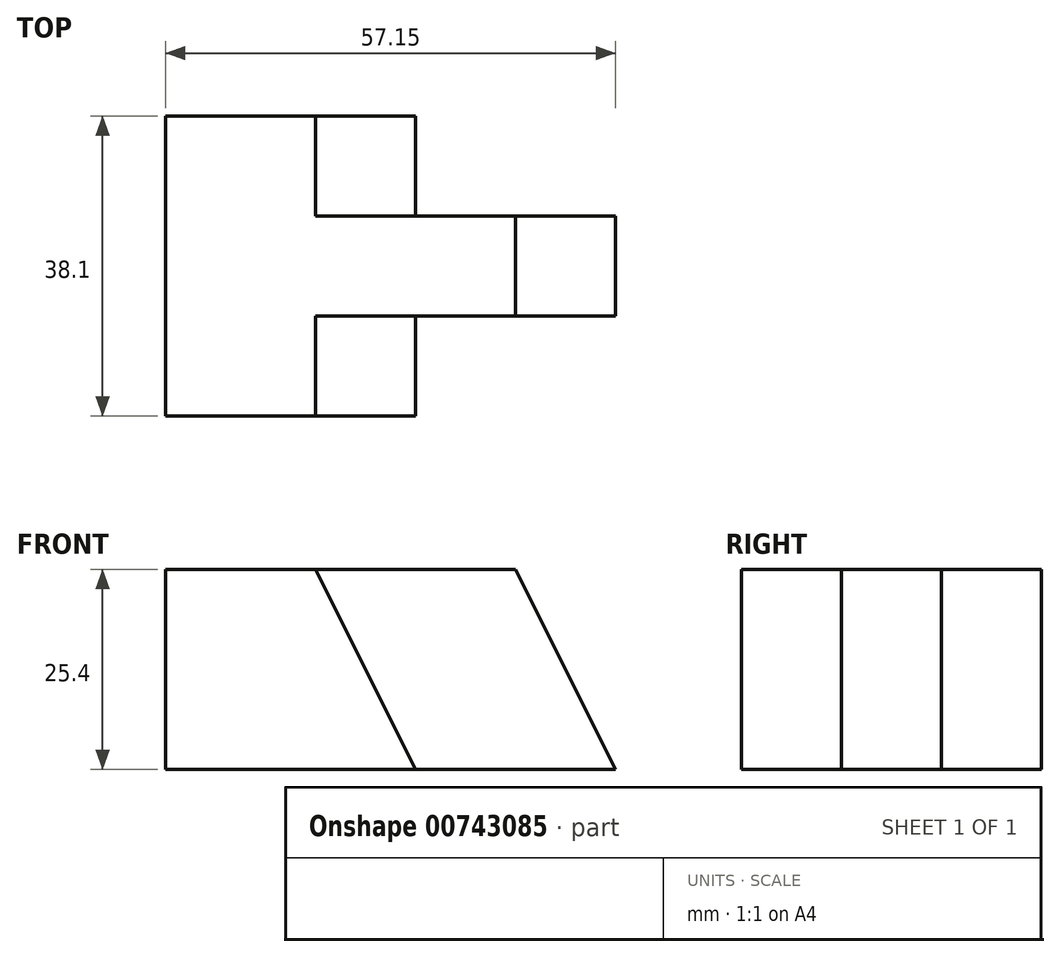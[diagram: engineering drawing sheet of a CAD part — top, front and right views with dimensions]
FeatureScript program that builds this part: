
annotation { "Feature Type Name" : "Feature", "Feature Type Description" : "" }
export const myFeature = defineFeature(function(context is Context, id is Id, definition is map)
    precondition{}
    {
        {
            var Q0;
            Q0=qCreatedBy(makeId("Front.planeOp"),FACE);
            var sketch = newSketch(context, id + "F0", { "sketchPlane" : qUnion([Q0])});
            skLineSegment(sketch, "E0", {"start": v(0, 0) * mm, "end": v(57.15, 0) * mm});
            skLineSegment(sketch, "E1", {"start": v(57.15, 0) * mm, "end": v(57.15, 25.4) * mm});
            skLineSegment(sketch, "E2", {"start": v(57.15, 25.4) * mm, "end": v(0, 25.4) * mm});
            skLineSegment(sketch, "E3", {"start": v(0, 25.4) * mm, "end": v(0, 0) * mm});
            skSolve(sketch);
        }
        {
            var Q0;
            Q0=makeQuery(id+"F0.imprint","IMPRINT",FACE,{"disambiguationData":[TD([[makeQuery(id+"F0.imprint","IMPRINT",EDGE,{"derivedFrom":sQuery(id+"F0.wireOp",EDGE,"E0")}),1.0]])]});
            extrude(context, id + "F1", {"entities" : qUnion([Q0]), "depth" : 38.1 * mm, "offsetDistance" : 25.4 * mm});
        }
        {
            var Q0;
            Q0=makeQuery(id+"F1.opExtrude","CAP_FACE",FACE,{"disambiguationData":[OSD([sQuery(id+"F0.wireOp",EDGE,"E0"),sQuery(id+"F0.wireOp",EDGE,"E1"),sQuery(id+"F0.wireOp",EDGE,"E2"),sQuery(id+"F0.wireOp",EDGE,"E3")])],"isStart":false});
            var sketch = newSketch(context, id + "F2", { "sketchPlane" : qUnion([Q0])});
            skLineSegment(sketch, "E4", {"start": v(19.05, 25.4) * mm, "end": v(31.75, 0) * mm});
            skSolve(sketch);
        }
        {
            var Q0;
            Q0 = qSketchRegion(id + "F0", true);
            extrude(context, id + "F3", {"entities" : qUnion([Q0]), "operationType" : NewBodyOperationType.ADD, "depth" : 25.4 * mm, "offsetDistance" : 25.4 * mm});
        }
        {
            var Q0;
            Q0 = qSketchRegion(id + "F2", true);
            var Q1;
            {var subQ0=sQuery(id+"F2.wireOp",EDGE,"E4");Q1=makeQuery(id+"F2.imprint","IMPRINT",FACE,{"disambiguationData":[TD([[makeQuery(id+"F2.imprint","IMPRINT",EDGE,{"derivedFrom":subQ0}),1.0]])]});}
            extrude(context, id + "F4", {"entities" : qUnion([Q0, Q1]), "operationType" : NewBodyOperationType.REMOVE, "oppositeDirection" : true, "depth" : 12.7 * mm, "offsetDistance" : 25.4 * mm});
        }
        {
            var Q0;
            Q0=makeQuery(id+"F1.opExtrude","CAP_FACE",FACE,{"disambiguationData":[OSD([sQuery(id+"F0.wireOp",EDGE,"E0"),sQuery(id+"F0.wireOp",EDGE,"E1"),sQuery(id+"F0.wireOp",EDGE,"E2"),sQuery(id+"F0.wireOp",EDGE,"E3")])],"isStart":true});
            var sketch = newSketch(context, id + "F5", { "sketchPlane" : qUnion([Q0])});
            skLineSegment(sketch, "E5", {"start": v(-19.05, 25.4) * mm, "end": v(-31.75, 0) * mm});
            skSolve(sketch);
        }
        {
            var Q0;
            {var subQ0=sQuery(id+"F5.wireOp",EDGE,"E5");Q0=makeQuery(id+"F5.imprint","IMPRINT",FACE,{"disambiguationData":[TD([[makeQuery(id+"F5.imprint","IMPRINT",EDGE,{"derivedFrom":subQ0}),-1.0]])]});}
            extrude(context, id + "F6", {"entities" : qUnion([Q0]), "operationType" : NewBodyOperationType.REMOVE, "oppositeDirection" : true, "depth" : 12.7 * mm, "offsetDistance" : 25.4 * mm});
        }
        {
            var Q0;
            Q0=makeQuery(id+"F4.boolean.opBoolean","COPY",FACE,{"derivedFrom":makeQuery(id+"F4.opExtrude","CAP_FACE",FACE,{"disambiguationData":[OSD([sQuery(id+"F0.wireOp",EDGE,"E0"),sQuery(id+"F0.wireOp",EDGE,"E1"),sQuery(id+"F0.wireOp",EDGE,"E2"),sQuery(id+"F2.wireOp",EDGE,"E4")])],"isStart":false})});
            var sketch = newSketch(context, id + "F7", { "sketchPlane" : qUnion([Q0])});
            skLineSegment(sketch, "E6", {"start": v(44.45, 25.4) * mm, "end": v(57.15, 0) * mm});
            skSolve(sketch);
        }
        {
            var Q0;
            Q0 = qSketchRegion(id + "F7", true);
            var Q1;
            {var subQ0=sQuery(id+"F7.wireOp",EDGE,"E6");Q1=makeQuery(id+"F7.imprint","IMPRINT",FACE,{"disambiguationData":[TD([[makeQuery(id+"F7.imprint","IMPRINT",EDGE,{"derivedFrom":subQ0}),1.0]])]});}
            extrude(context, id + "F8", {"entities" : qUnion([Q0, Q1]), "operationType" : NewBodyOperationType.REMOVE, "oppositeDirection" : true, "depth" : 25.4 * mm, "offsetDistance" : 25.4 * mm});
        }
    });
